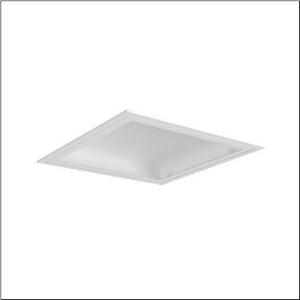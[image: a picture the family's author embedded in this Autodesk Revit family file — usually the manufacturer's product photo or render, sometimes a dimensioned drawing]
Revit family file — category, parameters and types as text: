
# Revit family: mira_r__21_51fr427a472a_c216
name_source: partatom
category: Lighting Fixtures
units: mm (PartAtom-declared; Revit-internal decimal feet)

## family parameters
Cut with Voids When Loaded = No
Host = Face
Light Source = No
Part Type = Normal
Room Calculation Point = No
Round Connector Dimension = Use Diameter
Shared = No

## types (1)
- Mira® 21 (1 x LED, 7680 lm, 66 W, 4000K)
    Apparent Load = 66 VA
    CIE Flux Codes = 50 81 97 100 100
    Color Rendering = 80
    Color Temperature = 4000K
    Default Elevation = 1800 mm
    Description = Mira® 21, clean room luminaire, primary light control with reflector, primary optical cover: cover, of PC, light emission: direct distribution, primary light characteristic: symmetric, installation type: recessed, LED, rated luminous flux: 7.680lm, luminous efficacy: 116lm/W, light colour: 840, colour temperature: 4000K, control gear: ON/OFF, with terminal, 3-pole, max. 2.5mm², mains connection: 230V, AC, 50/60Hz, rated input power: 66W, luminaire housing, of sheet steel, coated, pure white (RAL 9010), with concealed spring brackets, module: M625, length: 623mm, width: 623mm, height: 115mm, protection rating (complete): IP54, insulation class (complete): insulation class I (protective earthing), certification: CE, UKCA, permissible operating ambient temperature: -5..+40°C, standard: EN 50419, packaging unit: 1 piece
    Height = 0 mm  [stored 0 ft]
    Lamp = 1 x LED
    Lamp Light Flux = 7680 lm
    Lamp Power = 66 W
    Lamp count = 1
    Length = 625 mm
    Luminous efficacy = 116 lm/W
    Manufacturer = Siteco
    ModVariant = No
    Model = 51FR427A472A
    Mounting Place = Ceiling
    Mounting Type = Recessed
    Number of Poles = 1
    OnlyDefault = Yes
    Power Factor = 1
    Product Name = Mira® 21
    Product group = clean room luminaire | ceiling recessed
    ProductGroupID = 402
    Protection Class = Protection class I
    Protection Degree = IP 54
    RLX_Detail_Level = 1
    RLX_Emergency_Light_Flux = 0 lm
    RLX_Emergency_Type = 0
    RLX_Emergency_Type_DB = No
    RlxData = <blob elided: 13397 chars, md5=b2a60d26>
    Socket = socket
    Standby Power = 0 W
    System Light Flux = 7680 lm
    System Power = 66 W
    Type Comments = Product without accessories
    Type Image = l_1007109.jpg
    URL = http://relux.com
    VarID = ---
    Voltage = 0 V
    Weight = 0.00 kg
    Width = 625 mm

note: [stored X ft] marks values corroborated as IEEE doubles in the binary element streams (Revit-internal decimal feet)

## geometry (parser evidence)
native form markers: Sweep x10
no freeform markers — native parametric forms only
